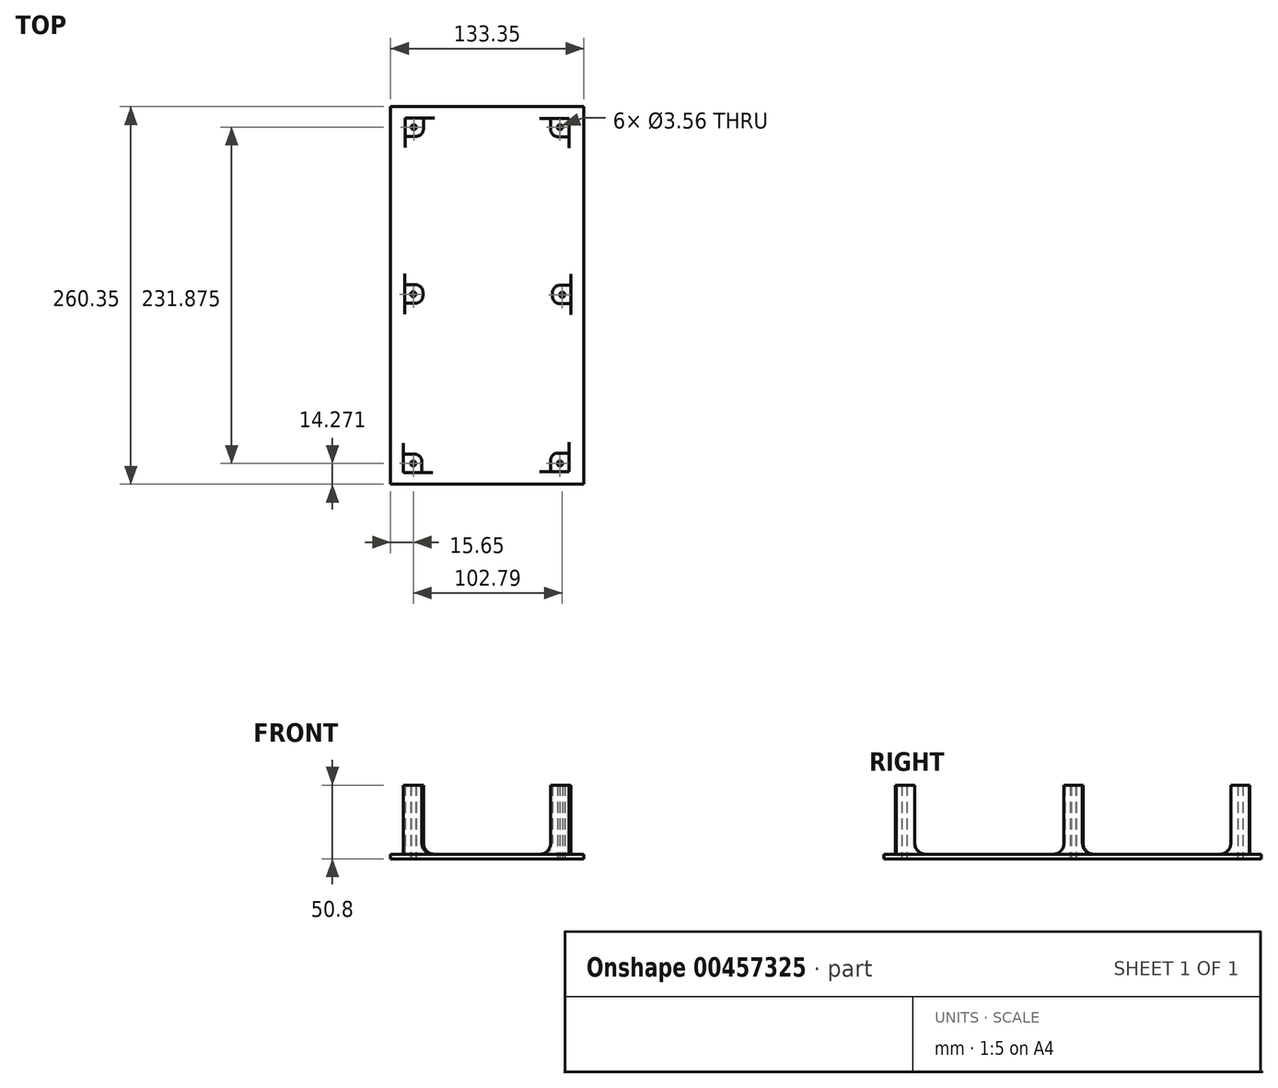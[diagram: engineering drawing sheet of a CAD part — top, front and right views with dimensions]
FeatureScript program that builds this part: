
annotation { "Feature Type Name" : "Feature", "Feature Type Description" : "" }
export const myFeature = defineFeature(function(context is Context, id is Id, definition is map)
    precondition{}
    {
        {
            var Q0;
            Q0=qCreatedBy(makeId("Top.planeOp"),FACE);
            var sketch = newSketch(context, id + "F0", { "sketchPlane" : qUnion([Q0])});
            skLineSegment(sketch, "E0.bottom", {"start": v(-61.02, 147.7) * mm, "end": v(72.33, 147.7) * mm});
            skLineSegment(sketch, "E0.top", {"start": v(-61.02, -112.66) * mm, "end": v(72.33, -112.66) * mm});
            skLineSegment(sketch, "E0.left", {"start": v(-61.02, 147.7) * mm, "end": v(-61.02, -112.66) * mm});
            skLineSegment(sketch, "E0.right", {"start": v(72.33, 147.7) * mm, "end": v(72.33, -112.66) * mm});
            skSolve(sketch);
        }
        {
            var Q0;
            Q0 = qSketchRegion(id + "F0", true);
            extrude(context, id + "F1", {"entities" : qUnion([Q0]), "depth" : 3.17 * mm});
        }
        {
            var Q0;
            Q0=qCreatedBy(makeId("Top.planeOp"),FACE);
            var sketch = newSketch(context, id + "F2", { "sketchPlane" : qUnion([Q0])});
            skLineSegment(sketch, "E1.bottom", {"start": v(-51.06, 139.89) * mm, "end": v(-38.36, 139.89) * mm});
            skLineSegment(sketch, "E1.top", {"start": v(-51.06, 127.19) * mm, "end": v(-38.36, 127.19) * mm});
            skLineSegment(sketch, "E1.left", {"start": v(-51.06, 139.89) * mm, "end": v(-51.06, 127.19) * mm});
            skLineSegment(sketch, "E1.right", {"start": v(-38.36, 139.89) * mm, "end": v(-38.36, 127.19) * mm});
            skLineSegment(sketch, "E2.bottom", {"start": v(49.45, 139.55) * mm, "end": v(62.15, 139.55) * mm});
            skLineSegment(sketch, "E2.top", {"start": v(49.45, 126.85) * mm, "end": v(62.15, 126.85) * mm});
            skLineSegment(sketch, "E2.left", {"start": v(49.45, 139.55) * mm, "end": v(49.45, 126.85) * mm});
            skLineSegment(sketch, "E2.right", {"start": v(62.15, 139.55) * mm, "end": v(62.15, 126.85) * mm});
            skLineSegment(sketch, "E3.bottom", {"start": v(49.45, -91.22) * mm, "end": v(62.15, -91.22) * mm});
            skLineSegment(sketch, "E3.top", {"start": v(49.45, -103.92) * mm, "end": v(62.15, -103.92) * mm});
            skLineSegment(sketch, "E3.left", {"start": v(49.45, -91.22) * mm, "end": v(49.45, -103.92) * mm});
            skLineSegment(sketch, "E3.right", {"start": v(62.15, -91.22) * mm, "end": v(62.15, -103.92) * mm});
            skLineSegment(sketch, "E4.bottom", {"start": v(-52.1, -92.01) * mm, "end": v(-39.4, -92.01) * mm});
            skLineSegment(sketch, "E4.top", {"start": v(-52.1, -104.71) * mm, "end": v(-39.4, -104.71) * mm});
            skLineSegment(sketch, "E4.left", {"start": v(-52.1, -92.01) * mm, "end": v(-52.1, -104.71) * mm});
            skLineSegment(sketch, "E4.right", {"start": v(-39.4, -92.01) * mm, "end": v(-39.4, -104.71) * mm});
            skLineSegment(sketch, "E5.bottom", {"start": v(50.7, 24.47) * mm, "end": v(63.4, 24.47) * mm});
            skLineSegment(sketch, "E5.top", {"start": v(50.7, 11.77) * mm, "end": v(63.4, 11.77) * mm});
            skLineSegment(sketch, "E5.left", {"start": v(50.7, 24.47) * mm, "end": v(50.7, 11.77) * mm});
            skLineSegment(sketch, "E5.right", {"start": v(63.4, 24.47) * mm, "end": v(63.4, 11.77) * mm});
            skLineSegment(sketch, "E6.bottom", {"start": v(-51.4, 24.8) * mm, "end": v(-38.7, 24.8) * mm});
            skLineSegment(sketch, "E6.top", {"start": v(-51.4, 12.1) * mm, "end": v(-38.7, 12.1) * mm});
            skLineSegment(sketch, "E6.left", {"start": v(-51.4, 24.8) * mm, "end": v(-51.4, 12.1) * mm});
            skLineSegment(sketch, "E6.right", {"start": v(-38.7, 24.8) * mm, "end": v(-38.7, 12.1) * mm});
            skSolve(sketch);
        }
        {
            var Q0;
            Q0 = qSketchRegion(id + "F2", true);
            extrude(context, id + "F3", {"entities" : qUnion([Q0]), "operationType" : NewBodyOperationType.ADD, "depth" : 50.8 * mm});
        }
        {
            var Q0;
            Q0=qCreatedBy(makeId("Top.planeOp"),FACE);
            var sketch = newSketch(context, id + "F4", { "sketchPlane" : qUnion([Q0])});
            skCircle(sketch, "E7", {"center": v(-44.97, 133.49) * mm, "radius": 1.78 * mm});
            skCircle(sketch, "E8", {"center": v(55.83, 133.49) * mm, "radius": 1.78 * mm});
            skCircle(sketch, "E9", {"center": v(-45.37, 18.35) * mm, "radius": 1.78 * mm});
            skCircle(sketch, "E10", {"center": v(57.42, 17.95) * mm, "radius": 1.78 * mm});
            skCircle(sketch, "E11", {"center": v(-45.37, -98.39) * mm, "radius": 1.78 * mm});
            skCircle(sketch, "E12", {"center": v(55.83, -98.39) * mm, "radius": 1.78 * mm});
            skSolve(sketch);
        }
        {
            var Q0;
            Q0 = qSketchRegion(id + "F4", true);
            extrude(context, id + "F5", {"entities" : qUnion([Q0]), "operationType" : NewBodyOperationType.REMOVE, "depth" : 101.6 * mm});
        }
        {
            var Q0;
            Q0=makeQuery(id+"F3.opExtrude","SWEPT_EDGE",EDGE,{"disambiguationData":[OSD([sQuery(id+"F2.wireOp",EDGE,"E1.top"),sQuery(id+"F2.wireOp",EDGE,"E1.right")])]});
            var Q1;
            Q1=makeQuery(id+"F3.opExtrude","SWEPT_EDGE",EDGE,{"disambiguationData":[OSD([sQuery(id+"F2.wireOp",EDGE,"E6.bottom"),sQuery(id+"F2.wireOp",EDGE,"E6.right")])]});
            var Q2;
            Q2=makeQuery(id+"F3.opExtrude","SWEPT_EDGE",EDGE,{"disambiguationData":[OSD([sQuery(id+"F2.wireOp",EDGE,"E6.top"),sQuery(id+"F2.wireOp",EDGE,"E6.right")])]});
            var Q3;
            Q3=makeQuery(id+"F3.opExtrude","SWEPT_EDGE",EDGE,{"disambiguationData":[OSD([sQuery(id+"F2.wireOp",EDGE,"E4.bottom"),sQuery(id+"F2.wireOp",EDGE,"E4.right")])]});
            var Q4;
            Q4=makeQuery(id+"F3.opExtrude","SWEPT_EDGE",EDGE,{"disambiguationData":[OSD([sQuery(id+"F2.wireOp",EDGE,"E2.top"),sQuery(id+"F2.wireOp",EDGE,"E2.left")])]});
            var Q5;
            Q5=makeQuery(id+"F3.opExtrude","SWEPT_EDGE",EDGE,{"disambiguationData":[OSD([sQuery(id+"F2.wireOp",EDGE,"E5.bottom"),sQuery(id+"F2.wireOp",EDGE,"E5.left")])]});
            var Q6;
            Q6=makeQuery(id+"F3.opExtrude","SWEPT_EDGE",EDGE,{"disambiguationData":[OSD([sQuery(id+"F2.wireOp",EDGE,"E3.bottom"),sQuery(id+"F2.wireOp",EDGE,"E3.left")])]});
            var Q7;
            Q7=makeQuery(id+"F3.opExtrude","SWEPT_EDGE",EDGE,{"disambiguationData":[OSD([sQuery(id+"F2.wireOp",EDGE,"E5.top"),sQuery(id+"F2.wireOp",EDGE,"E5.left")])]});
            fillet(context, id + "F6", {"entities" : qUnion([Q0, Q1, Q2, Q3, Q4, Q5, Q6, Q7]), "radius" : 5.08 * mm, "tangentPropagation" : true, "allowEdgeOverflow" : false});
        }
        {
            var Q0;
            Q0=makeQuery(id+"F3.boolean.opBoolean","INTERSECT",EDGE,{"derivedFrom":[makeQuery(id+"F1.opExtrude","CAP_FACE",FACE,{"disambiguationData":[OSD([sQuery(id+"F0.wireOp",EDGE,"E0.bottom"),sQuery(id+"F0.wireOp",EDGE,"E0.top"),sQuery(id+"F0.wireOp",EDGE,"E0.left"),sQuery(id+"F0.wireOp",EDGE,"E0.right")])],"isStart":false}),makeQuery(id+"F3.opExtrude","SWEPT_FACE",FACE,{"disambiguationData":[OSD([sQuery(id+"F2.wireOp",EDGE,"E1.top")])]})]});
            var Q1;
            Q1=makeQuery(id+"F6.opFillet","BLEND_EDGE",EDGE,{"blendedFrom":[makeQuery(id+"F3.opExtrude","SWEPT_EDGE",EDGE,{"disambiguationData":[OSD([sQuery(id+"F2.wireOp",EDGE,"E2.top"),sQuery(id+"F2.wireOp",EDGE,"E2.left")])]}),makeQuery(id+"F1.opExtrude","CAP_FACE",FACE,{"disambiguationData":[OSD([sQuery(id+"F0.wireOp",EDGE,"E0.bottom"),sQuery(id+"F0.wireOp",EDGE,"E0.top"),sQuery(id+"F0.wireOp",EDGE,"E0.left"),sQuery(id+"F0.wireOp",EDGE,"E0.right")])],"isStart":false})],"blendedInto":[makeQuery(id+"F1.opExtrude","CAP_FACE",FACE,{"disambiguationData":[OSD([sQuery(id+"F0.wireOp",EDGE,"E0.bottom"),sQuery(id+"F0.wireOp",EDGE,"E0.top"),sQuery(id+"F0.wireOp",EDGE,"E0.left"),sQuery(id+"F0.wireOp",EDGE,"E0.right")])],"isStart":false})]});
            var Q2;
            Q2=makeQuery(id+"F6.opFillet","BLEND_EDGE",EDGE,{"blendedFrom":[makeQuery(id+"F3.opExtrude","SWEPT_EDGE",EDGE,{"disambiguationData":[OSD([sQuery(id+"F2.wireOp",EDGE,"E6.top"),sQuery(id+"F2.wireOp",EDGE,"E6.right")])]}),makeQuery(id+"F1.opExtrude","CAP_FACE",FACE,{"disambiguationData":[OSD([sQuery(id+"F0.wireOp",EDGE,"E0.bottom"),sQuery(id+"F0.wireOp",EDGE,"E0.top"),sQuery(id+"F0.wireOp",EDGE,"E0.left"),sQuery(id+"F0.wireOp",EDGE,"E0.right")])],"isStart":false})],"blendedInto":[makeQuery(id+"F1.opExtrude","CAP_FACE",FACE,{"disambiguationData":[OSD([sQuery(id+"F0.wireOp",EDGE,"E0.bottom"),sQuery(id+"F0.wireOp",EDGE,"E0.top"),sQuery(id+"F0.wireOp",EDGE,"E0.left"),sQuery(id+"F0.wireOp",EDGE,"E0.right")])],"isStart":false})]});
            var Q3;
            Q3=makeQuery(id+"F6.opFillet","BLEND_EDGE",EDGE,{"blendedFrom":[makeQuery(id+"F3.opExtrude","SWEPT_EDGE",EDGE,{"disambiguationData":[OSD([sQuery(id+"F2.wireOp",EDGE,"E5.top"),sQuery(id+"F2.wireOp",EDGE,"E5.left")])]}),makeQuery(id+"F1.opExtrude","CAP_FACE",FACE,{"disambiguationData":[OSD([sQuery(id+"F0.wireOp",EDGE,"E0.bottom"),sQuery(id+"F0.wireOp",EDGE,"E0.top"),sQuery(id+"F0.wireOp",EDGE,"E0.left"),sQuery(id+"F0.wireOp",EDGE,"E0.right")])],"isStart":false})],"blendedInto":[makeQuery(id+"F1.opExtrude","CAP_FACE",FACE,{"disambiguationData":[OSD([sQuery(id+"F0.wireOp",EDGE,"E0.bottom"),sQuery(id+"F0.wireOp",EDGE,"E0.top"),sQuery(id+"F0.wireOp",EDGE,"E0.left"),sQuery(id+"F0.wireOp",EDGE,"E0.right")])],"isStart":false})]});
            var Q4;
            Q4=makeQuery(id+"F3.boolean.opBoolean","INTERSECT",EDGE,{"derivedFrom":[makeQuery(id+"F1.opExtrude","CAP_FACE",FACE,{"disambiguationData":[OSD([sQuery(id+"F0.wireOp",EDGE,"E0.bottom"),sQuery(id+"F0.wireOp",EDGE,"E0.top"),sQuery(id+"F0.wireOp",EDGE,"E0.left"),sQuery(id+"F0.wireOp",EDGE,"E0.right")])],"isStart":false}),makeQuery(id+"F3.opExtrude","SWEPT_FACE",FACE,{"disambiguationData":[OSD([sQuery(id+"F2.wireOp",EDGE,"E4.right")])]})]});
            var Q5;
            Q5=makeQuery(id+"F3.boolean.opBoolean","INTERSECT",EDGE,{"derivedFrom":[makeQuery(id+"F1.opExtrude","CAP_FACE",FACE,{"disambiguationData":[OSD([sQuery(id+"F0.wireOp",EDGE,"E0.bottom"),sQuery(id+"F0.wireOp",EDGE,"E0.top"),sQuery(id+"F0.wireOp",EDGE,"E0.left"),sQuery(id+"F0.wireOp",EDGE,"E0.right")])],"isStart":false}),makeQuery(id+"F3.opExtrude","SWEPT_FACE",FACE,{"disambiguationData":[OSD([sQuery(id+"F2.wireOp",EDGE,"E3.left")])]})]});
            fillet(context, id + "F7", {"entities" : qUnion([Q0, Q1, Q2, Q3, Q4, Q5]), "radius" : 7.62 * mm, "tangentPropagation" : true, "allowEdgeOverflow" : false});
        }
    });
